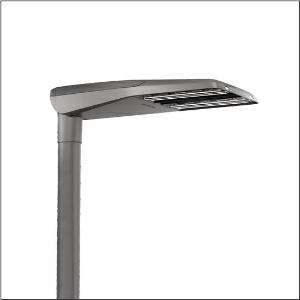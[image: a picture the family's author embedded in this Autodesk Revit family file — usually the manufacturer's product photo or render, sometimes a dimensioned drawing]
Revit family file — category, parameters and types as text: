
# Revit family: streetlight_sl_11_iq_midi___st1_2a_5xc3a51e08le_ac55
name_source: partatom
category: Lighting Fixtures
units: mm (PartAtom-declared; Revit-internal decimal feet)

## family parameters
Cut with Voids When Loaded = No
Host = Face
Light Source = No
Part Type = Normal
Room Calculation Point = No
Round Connector Dimension = Use Diameter
Shared = No

## types (1)
- --- (1 x LED, 9210 lm, 60.4 W, 3000K)
    Apparent Load = 60 VA
    CIE Flux Codes = 32 70 96 100 100
    Color Rendering = 70
    Color Temperature = 3000K
    Default Elevation = 1800 mm
    Description = Streetlight SL 11 iQ midi, mast luminaire, primary light control with 3 zone facetted reflector, of plastic, silver coated, highly specular, primary optical cover: cover, of PMMA, transparent, light distribution: ST1.2a, light emission: direct distribution, primary light characteristic: asymmetric, installation type: post-top, side-entry, LED, High Power LED, rated luminous flux: 9.210lm, luminous efficacy: 153lm/W, light colour: 730, colour temperature: 3000K, control: optimised constant luminous flux control (CLO 2.0), Desk-Remote (wireless, voltage-free reading and setting of iQ features in the workshop via application-optimized NFC function/RFID function), Light-Fading, Smart-Wire, Night-Set, Lumen-Switch, Temp-Guard, Auto-Match, with cable H07RN-F 5x 1.5mm², mains connection: 230..240V, AC, 50/60Hz, connection cable pre-assembled, cable length: 8,5m, start of lifetime: 60W, end of service life: 63W, reduction: 30W, luminaire housing, of diecast aluminium, powder-coated, Siteco® metallic grey (DB 702S), please order mast flange separately, inclination adjustable without tools: 0°, 5°, 10°, 15° (post-top) | 0°, -5°, -10°, -15° (side-entry), sealing non-destructively replaceable, multi-level sealing system, length: 780mm, width: 376mm, height: 118mm, mast flange for spigot size: 42mm (side-entry): 5XC10008XM4, 60/48mm (side-entry/post-top): 5XC10108XM2, 76/60mm (side-entry/post-top): 5XC10108XM1, equipment: standard, protection rating (complete): IP66, insulation class (complete): insulation class II (safety insulation), certification: CE, ENEC, VDE, impact resistance: IK09, permissible operating ambient temperature for outdoor applications: -25..+50°C, standard-compliant lighting for roads and squares, Environmental Product Declaration (EPD) tested and certified by an independent institute, packaging unit: 1 piece

Light Distribution: ST1.2a
    Height = 118 mm
    Lamp = 1 x LED
    Lamp Light Flux = 9210 lm
    Lamp Power = 60.4 W
    Lamp count = 1
    Length = 780 mm
    Luminous efficacy = 152 lm/W
    Manufacturer = Siteco
    ModVariant = No
    Model = 5XC3A51E08LE
    Number of Poles = 1
    OnlyDefault = Yes
    Power Factor = 1
    Product Name = Streetlight SL 11 iQ midi | ST1.2a
    Product group = mast luminaire | pylon top
    ProductGroupID = 6100
    Protection Class = Protection class II
    Protection Degree = IP 66
    RLX_Detail_Level = 1
    RLX_Emergency_Light_Flux = 0 lm
    RLX_Emergency_Type = 0
    RLX_Emergency_Type_DB = No
    RlxData = <blob elided: 70601 chars, md5=cf25cc18>
    Socket = socket
    Standby Power = 0 W
    System Light Flux = 9210 lm
    System Power = 60 W
    Type Comments = factory setting: luminous flux: 100 % | dim-lin: 254 | 520 mA
    Type Image = l_1005960.jpg
    URL = http://relux.com
    VarID = @adj_150753
    Voltage = 0 V
    Weight = 0.00 kg
    Width = 376 mm

## geometry (parser evidence)
native form markers: Blend x4, Sweep x9
no freeform markers — native parametric forms only
